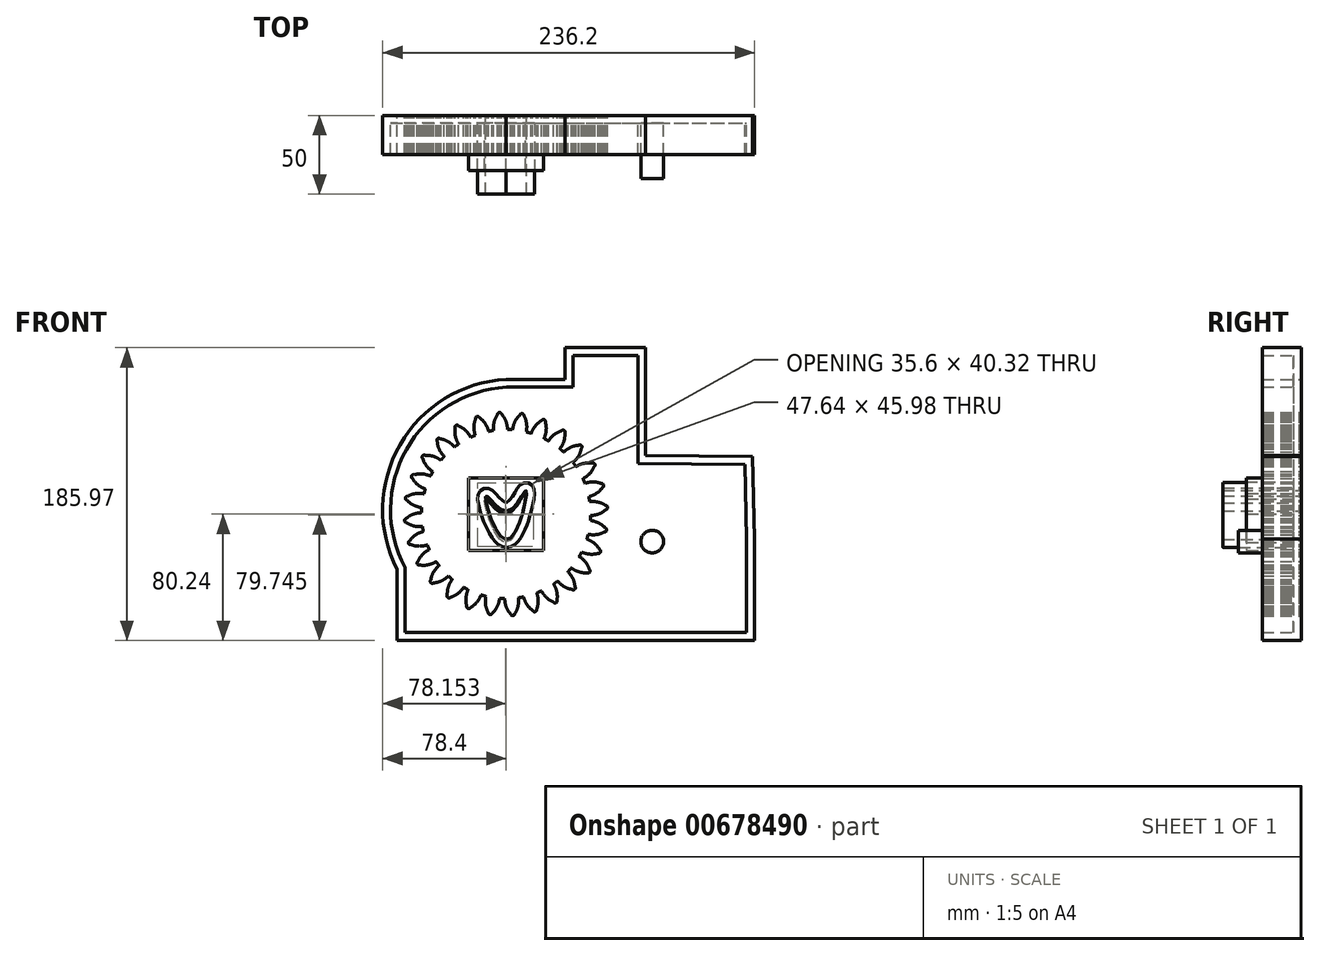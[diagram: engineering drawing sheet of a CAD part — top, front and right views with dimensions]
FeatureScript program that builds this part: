
annotation { "Feature Type Name" : "Feature", "Feature Type Description" : "" }
export const myFeature = defineFeature(function(context is Context, id is Id, definition is map)
    precondition{}
    {
        {
            var Q0;
            Q0=qCreatedBy(makeId("Front.planeOp"),FACE);
            var sketch = newSketch(context, id + "F0", { "sketchPlane" : qUnion([Q0])});
            skCircle(sketch, "E0", {"center": v(0, 0) * mm, "radius": 53.72 * mm});
            skCircle(sketch, "E1", {"center": v(0, 0) * mm, "radius": 58.67 * mm, "construction": true});
            skCircle(sketch, "E2", {"center": v(0, 0) * mm, "radius": 63.5 * mm, "construction": true});
            skLineSegment(sketch, "E3", {"start": v(0, 0) * mm, "end": v(0, 72.67) * mm, "construction": true});
            skLineSegment(sketch, "E4", {"start": v(0, 0) * mm, "end": v(-5.05, 77.02) * mm, "construction": true});
            skLineSegment(sketch, "E5", {"start": v(0, 58.67) * mm, "end": v(-57.47, 58.67) * mm, "construction": true});
            skLineSegment(sketch, "E6", {"start": v(0, 58.67) * mm, "end": v(-61.26, 36.38) * mm, "construction": true});
            skCircle(sketch, "E7", {"center": v(0, 0) * mm, "radius": 55.14 * mm, "construction": true});
            skCircle(sketch, "E8", {"center": v(0, 58.67) * mm, "radius": 14.6 * mm, "construction": true});
            skCircle(sketch, "E9", {"center": v(-13.72, 53.68) * mm, "radius": 14.6 * mm, "construction": true});
            skArc(sketch, "E10", {"start": v(0, 58.67) * mm, "mid": v(-1.19, 61.2) * mm, "end": v(-2.86, 63.44) * mm});
            skArc(sketch, "E11", {"start": v(0.88, 53.71) * mm, "mid": v(0.64, 56.23) * mm, "end": v(0, 58.67) * mm});
            skArc(sketch, "E12.MirrorCS", {"start": v(-7.66, 58.17) * mm, "mid": v(-6.8, 60.83) * mm, "end": v(-5.45, 63.27) * mm});
            skArc(sketch, "E13.MirrorCS", {"start": v(-7.88, 53.14) * mm, "mid": v(-7.98, 55.66) * mm, "end": v(-7.66, 58.17) * mm});
            skArc(sketch, "E14", {"start": v(-2.86, 63.44) * mm, "mid": v(-4.23, 64.55) * mm, "end": v(-5.45, 63.27) * mm});
            skLineSegment(sketch, "E15.bottom", {"start": v(-23.82, 23) * mm, "end": v(23.82, 23) * mm});
            skLineSegment(sketch, "E15.top", {"start": v(-23.82, -23) * mm, "end": v(23.82, -23) * mm});
            skLineSegment(sketch, "E15.left", {"start": v(-23.82, 23) * mm, "end": v(-23.82, -23) * mm});
            skLineSegment(sketch, "E15.right", {"start": v(23.82, 23) * mm, "end": v(23.82, -23) * mm});
            skFitSpline(sketch, "E16", {"points": [v(0, 0) * mm, v(12.25, 13.08) * mm, v(0, -18.04) * mm, v(-13.35, 9.5) * mm, v(0, 0) * mm]});
            skSolve(sketch);
        }
        {
            var Q0;
            {var subQ0=sQuery(id+"F0.wireOp",EDGE,"E0");var subQ1=makeQuery(id+"F0.imprint","INTERSECT",VERTEX,{"derivedFrom":[subQ0,sQuery(id+"F0.wireOp",EDGE,"E11")]});Q0=makeQuery(id+"F0.imprint","IMPRINT",FACE,{"disambiguationData":[TD([[makeQuery(id+"F0.imprint","IMPRINT",EDGE,{"disambiguationData":[TD([[subQ1,-1.0]])],"derivedFrom":subQ0}),1.0]])]});}
            var Q1;
            Q1=makeQuery(id+"F0.imprint","IMPRINT",FACE,{"disambiguationData":[TD([[makeQuery(id+"F0.imprint","IMPRINT",EDGE,{"derivedFrom":sQuery(id+"F0.wireOp",EDGE,"E10")}),1.0]])]});
            extrude(context, id + "F1", {"entities" : qUnion([Q0, Q1]), "depth" : 25 * mm, "offsetDistance" : 25 * mm});
        }
        {
            var Q0;
            Q0=makeQuery(id+"F1.opExtrude","SWEPT_BODY",BODY,{"disambiguationData":[OSD([sQuery(id+"F0.wireOp",EDGE,"E0"),sQuery(id+"F0.wireOp",EDGE,"E10"),sQuery(id+"F0.wireOp",EDGE,"E11"),sQuery(id+"F0.wireOp",EDGE,"E12.MirrorCS"),sQuery(id+"F0.wireOp",EDGE,"E13.MirrorCS"),sQuery(id+"F0.wireOp",EDGE,"E14")])]});
            var Q1;
            Q1=makeQuery(id+"F1.opExtrude","SWEPT_FACE",FACE,{"disambiguationData":[OSD([sQuery(id+"F0.wireOp",EDGE,"E0")])]});
            circularPattern(context, id + "F2", {"entities" : qUnion([Q0]), "axis" : qUnion([Q1]), "angle" : 360 * degree, "instanceCount" : 28, "equalSpace" : true});
        }
        {
            var Q0;
            Q0=makeQuery(id+"F0.imprint","IMPRINT",FACE,{"disambiguationData":[TD([[makeQuery(id+"F0.imprint","IMPRINT",EDGE,{"derivedFrom":sQuery(id+"F0.wireOp",EDGE,"E15.bottom")}),-1.0]])]});
            extrude(context, id + "F3", {"entities" : qUnion([Q0]), "operationType" : NewBodyOperationType.ADD, "depth" : 35 * mm, "offsetDistance" : 25 * mm});
        }
        {
            var Q0;
            Q0=qCreatedBy(makeId("Front.planeOp"),FACE);
            var sketch = newSketch(context, id + "F4", { "sketchPlane" : qUnion([Q0])});
            skLineSegment(sketch, "E17", {"start": v(-69.3, -35.12) * mm, "end": v(-69.3, -80.24) * mm});
            skLineSegment(sketch, "E18", {"start": v(-69.3, -80.24) * mm, "end": v(157.8, -80.24) * mm});
            skLineSegment(sketch, "E19", {"start": v(157.8, -80.24) * mm, "end": v(157.8, -15.79) * mm});
            skArc(sketch, "E20", {"start": v(0, 85.57) * mm, "mid": v(-67.38, 44.02) * mm, "end": v(-69.3, -35.12) * mm});
            skLineSegment(sketch, "E21", {"start": v(0, 85.57) * mm, "end": v(37.45, 85.57) * mm});
            skLineSegment(sketch, "E22", {"start": v(37.45, 85.57) * mm, "end": v(37.45, 105.73) * mm});
            skLineSegment(sketch, "E23", {"start": v(37.45, 105.73) * mm, "end": v(88.7, 105.73) * mm});
            skLineSegment(sketch, "E24", {"start": v(88.7, 105.73) * mm, "end": v(88.7, 37.2) * mm});
            skLineSegment(sketch, "E25", {"start": v(88.7, 37.2) * mm, "end": v(156.65, 36.62) * mm});
            skLineSegment(sketch, "E26", {"start": v(156.65, 36.62) * mm, "end": v(157.8, -15.79) * mm});
            skFitSpline(sketch, "E27", {"points": [v(0.53, 1.9) * mm, v(12.79, 14.97) * mm, v(0.53, -16.14) * mm, v(-12.82, 11.4) * mm, v(0.53, 1.9) * mm]});
            skSolve(sketch);
        }
        {
            var Q0;
            Q0=makeQuery(id+"F4.imprint","IMPRINT",FACE,{"disambiguationData":[TD([[makeQuery(id+"F4.imprint","IMPRINT",EDGE,{"derivedFrom":sQuery(id+"F4.wireOp",EDGE,"E17")}),1.0]])]});
            extrude(context, id + "F5", {"entities" : qUnion([Q0]), "depth" : 50 * mm, "offsetDistance" : 25 * mm});
        }
        {
            var Q0;
            Q0=makeQuery(id+"F5.opExtrude","CAP_FACE",FACE,{"disambiguationData":[OSD([sQuery(id+"F4.wireOp",EDGE,"E17"),sQuery(id+"F4.wireOp",EDGE,"E18"),sQuery(id+"F4.wireOp",EDGE,"E19"),sQuery(id+"F4.wireOp",EDGE,"E20"),sQuery(id+"F4.wireOp",EDGE,"E21"),sQuery(id+"F4.wireOp",EDGE,"E22"),sQuery(id+"F4.wireOp",EDGE,"E23"),sQuery(id+"F4.wireOp",EDGE,"E24"),sQuery(id+"F4.wireOp",EDGE,"E25"),sQuery(id+"F4.wireOp",EDGE,"E26")])],"isStart":false});
            shell(context, id + "F6", {"entities" : qUnion([Q0]), "thickness" : 5 * mm});
        }
        {
            var Q0;
            Q0=makeQuery(id+"F5.opExtrude","CAP_FACE",FACE,{"disambiguationData":[OSD([sQuery(id+"F4.wireOp",EDGE,"E17"),sQuery(id+"F4.wireOp",EDGE,"E18"),sQuery(id+"F4.wireOp",EDGE,"E19"),sQuery(id+"F4.wireOp",EDGE,"E20"),sQuery(id+"F4.wireOp",EDGE,"E21"),sQuery(id+"F4.wireOp",EDGE,"E22"),sQuery(id+"F4.wireOp",EDGE,"E23"),sQuery(id+"F4.wireOp",EDGE,"E24"),sQuery(id+"F4.wireOp",EDGE,"E25"),sQuery(id+"F4.wireOp",EDGE,"E26"),sQuery(id+"F4.wireOp",EDGE,"E27")])],"isStart":false});
            extrude(context, id + "F7", {"entities" : qUnion([Q0]), "operationType" : NewBodyOperationType.REMOVE, "oppositeDirection" : true, "depth" : 25 * mm, "offsetDistance" : 25 * mm});
        }
        {
            var Q0;
            Q0=qCreatedBy(makeId("Front.planeOp"),FACE);
            var sketch = newSketch(context, id + "F8", { "sketchPlane" : qUnion([Q0])});
            skCircle(sketch, "E28", {"center": v(92.79, -17.47) * mm, "radius": 7.2 * mm});
            skSolve(sketch);
        }
        {
            var Q0;
            Q0 = qSketchRegion(id + "F8", true);
            extrude(context, id + "F9", {"entities" : qUnion([Q0]), "operationType" : NewBodyOperationType.ADD, "depth" : 40 * mm, "offsetDistance" : 25 * mm});
        }
    });
